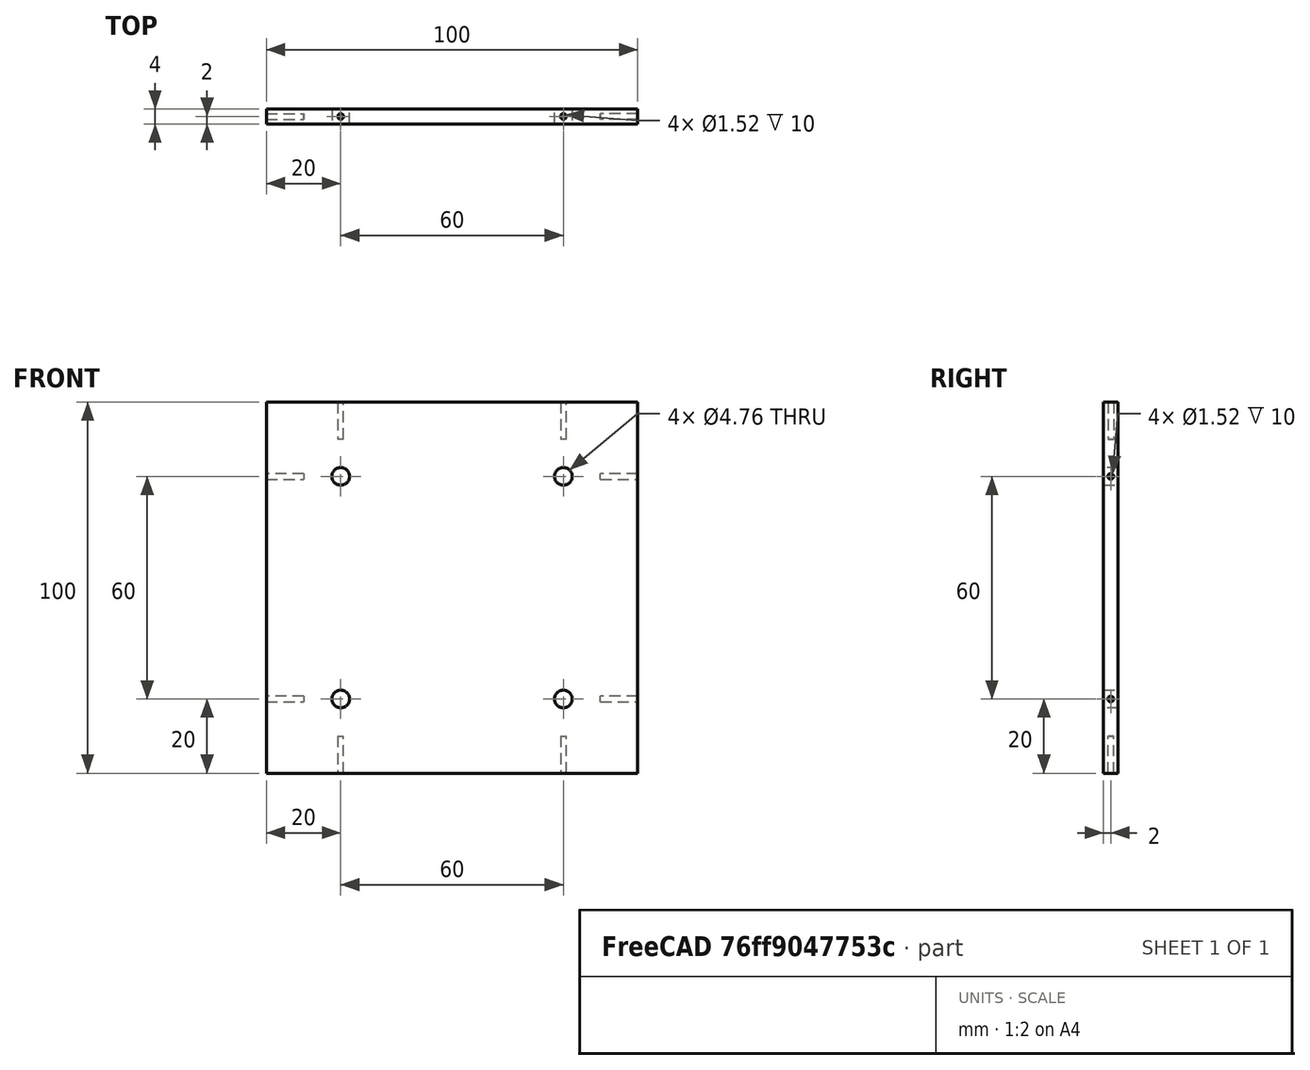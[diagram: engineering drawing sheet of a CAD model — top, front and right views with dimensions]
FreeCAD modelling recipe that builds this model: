
FCSTD DOCUMENT  (FreeCAD 0.20R29603 (Git))
Label: MechanicalCF35Mount002
License: All rights reserved
LicenseURL: http://en.wikipedia.org/wiki/All_rights_reserved
objects: Part::Cylinder×12, Part::Compound×9, TechDraw::DrawViewDimension×9, TechDraw::DrawProjGroupItem×5, Part::Cut×2, Part::Box×1, Part::Feature×1, TechDraw::DrawSVGTemplate×1, TechDraw::DrawProjGroup×1, TechDraw::DrawPage×1
note: 25 computed .brp shape members not serialized (recipe doc carries the construction recipe); baked Part::Feature solids carry a one-line shape summary decoded from their .brp

FEATURE [Part::Box] Box  label="Würfel"
  AttacherType = Attacher::AttachEngine3D
  Height = 100
  Length = 100
  Placement = pos=(-50,0,-50) rot=(0,0,1;0rad)
  Width = 4
FEATURE [Part::Cylinder] Cylinder011  label="Zylinder011"
  Angle = 360
  AttacherType = Attacher::AttachEngine3D
  FirstAngle = 0
  Height = 300
  Placement = pos=(30,12.7,30) rot=(1,0,0;1.5708rad)
  Radius = 2.38
  SecondAngle = 0
FEATURE [Part::Cylinder] Cylinder012  label="Zylinder012"
  Angle = 360
  AttacherType = Attacher::AttachEngine3D
  FirstAngle = 0
  Height = 300
  Placement = pos=(30,12.7,30) rot=(1,0,0;1.5708rad)
  Radius = 2.38
  SecondAngle = 0
FEATURE [Part::Compound] Compound008
  Links = -> [Cylinder012]
  Placement = pos=(0,0,0) rot=(0,1,0;1.5708rad)
FEATURE [Part::Cylinder] Cylinder013  label="Zylinder013"
  Angle = 360
  AttacherType = Attacher::AttachEngine3D
  FirstAngle = 0
  Height = 300
  Placement = pos=(30,12.7,30) rot=(1,0,0;1.5708rad)
  Radius = 2.38
  SecondAngle = 0
FEATURE [Part::Compound] Compound009
  Links = -> [Cylinder013]
  Placement = pos=(0,0,0) rot=(0,1,0;3.14159rad)
FEATURE [Part::Cylinder] Cylinder014  label="Zylinder014"
  Angle = 360
  AttacherType = Attacher::AttachEngine3D
  FirstAngle = 0
  Height = 300
  Placement = pos=(30,12.7,30) rot=(1,0,0;1.5708rad)
  Radius = 2.38
  SecondAngle = 0
FEATURE [Part::Compound] Compound010
  Links = -> [Cylinder014]
  Placement = pos=(0,0,0) rot=(0,-1,0;1.5708rad)
FEATURE [Part::Compound] Compound014  label="M6ThreadRods"
  Links = -> [Cylinder011,Compound008,Compound009,Compound010]
FEATURE [Part::Cut] Cut
  Base = -> Box
  Tool = -> Compound014
FEATURE [Part::Cylinder] Cylinder  label="Zylinder"
  Angle = 360
  AttacherType = Attacher::AttachEngine3D
  FirstAngle = 0
  Height = 10
  Placement = pos=(30,2,40) rot=(0,0,1;0rad)
  Radius = 0.76
  SecondAngle = 0
FEATURE [Part::Cylinder] Cylinder015  label="Zylinder015"
  Angle = 360
  AttacherType = Attacher::AttachEngine3D
  FirstAngle = 0
  Height = 10
  Placement = pos=(-30,2,40) rot=(0,0,1;0rad)
  Radius = 0.76
  SecondAngle = 0
FEATURE [Part::Compound] Compound
  Links = -> [Cylinder,Cylinder015]
FEATURE [Part::Cylinder] Cylinder016  label="Zylinder016"
  Angle = 360
  AttacherType = Attacher::AttachEngine3D
  FirstAngle = 0
  Height = 10
  Placement = pos=(30,2,40) rot=(0,0,1;0rad)
  Radius = 0.76
  SecondAngle = 0
FEATURE [Part::Cylinder] Cylinder017  label="Zylinder017"
  Angle = 360
  AttacherType = Attacher::AttachEngine3D
  FirstAngle = 0
  Height = 10
  Placement = pos=(-30,2,40) rot=(0,0,1;0rad)
  Radius = 0.76
  SecondAngle = 0
FEATURE [Part::Compound] Compound015
  Links = -> [Cylinder016,Cylinder017]
  Placement = pos=(0,0,0) rot=(0,1,0;1.5708rad)
FEATURE [Part::Cylinder] Cylinder018  label="Zylinder018"
  Angle = 360
  AttacherType = Attacher::AttachEngine3D
  FirstAngle = 0
  Height = 10
  Placement = pos=(30,2,40) rot=(0,0,1;0rad)
  Radius = 0.76
  SecondAngle = 0
FEATURE [Part::Cylinder] Cylinder019  label="Zylinder019"
  Angle = 360
  AttacherType = Attacher::AttachEngine3D
  FirstAngle = 0
  Height = 10
  Placement = pos=(-30,2,40) rot=(0,0,1;0rad)
  Radius = 0.76
  SecondAngle = 0
FEATURE [Part::Compound] Compound016
  Links = -> [Cylinder018,Cylinder019]
  Placement = pos=(0,0,0) rot=(0,1,0;3.14159rad)
FEATURE [Part::Cylinder] Cylinder020  label="Zylinder020"
  Angle = 360
  AttacherType = Attacher::AttachEngine3D
  FirstAngle = 0
  Height = 10
  Placement = pos=(30,2,40) rot=(0,0,1;0rad)
  Radius = 0.76
  SecondAngle = 0
FEATURE [Part::Cylinder] Cylinder021  label="Zylinder021"
  Angle = 360
  AttacherType = Attacher::AttachEngine3D
  FirstAngle = 0
  Height = 10
  Placement = pos=(-30,2,40) rot=(0,0,1;0rad)
  Radius = 0.76
  SecondAngle = 0
FEATURE [Part::Compound] Compound017
  Links = -> [Cylinder020,Cylinder021]
  Placement = pos=(0,0,0) rot=(0,-1,0;1.5708rad)
FEATURE [Part::Compound] Compound018  label="M2Corehole"
  Links = -> [Compound017,Compound,Compound015,Compound016]
FEATURE [Part::Cut] Cut001
  Base = -> Cut
  Tool = -> Compound018
FEATURE [Part::Feature] Cut001_solid  label="Cut001 (Solid)"
  shape: bbox 100 x 4 x 100 mm, 26 faces (baked)
FEATURE [TechDraw::DrawSVGTemplate] Template
  EditableTexts = Designed_by_Name=Thomas Spielauer; FC-Date=2023-07-05; FC-SC=mm; FC-SH=01; FC-Title=CF40 electronics housing; Subtitle=Backplate
  Height = 210
  Orientation = 1
  Width = 297
FEATURE [TechDraw::DrawProjGroupItem] ProjItem  label="Front"
  CoarseView = false
  Direction = (0,1,0)
  Focus = 100
  HardHidden = false
  IsoCount = 0
  IsoHidden = false
  IsoVisible = false
  LockPosition = true
  Perspective = false
  Rotation = 0
  RotationVector = (0,0,-1)
  ScaleType = 2
  SeamHidden = false
  SeamVisible = true
  SmoothHidden = false
  SmoothVisible = true
  Source = -> [Cut001]
  Type = 0
  X = 0
  XDirection = (0,0,-1)
  Y = 0
FEATURE [TechDraw::DrawProjGroupItem] ProjItem001  label="Right"
  CoarseView = false
  Direction = (0,1e-16,-1)
  Focus = 100
  HardHidden = false
  IsoCount = 0
  IsoHidden = false
  IsoVisible = false
  LockPosition = false
  Perspective = false
  Rotation = 0
  RotationVector = (1,0,0)
  ScaleType = 2
  SeamHidden = false
  SeamVisible = true
  SmoothHidden = false
  SmoothVisible = true
  Source = -> [Cut001]
  Type = 2
  X = -67.1947
  XDirection = (0,-1,-1e-16)
  Y = 0
FEATURE [TechDraw::DrawProjGroupItem] ProjItem002  label="Left"
  CoarseView = false
  Direction = (0,1e-16,1)
  Focus = 100
  HardHidden = false
  IsoCount = 0
  IsoHidden = false
  IsoVisible = false
  LockPosition = false
  Perspective = false
  Rotation = 0
  RotationVector = (1,0,0)
  ScaleType = 2
  SeamHidden = false
  SeamVisible = true
  SmoothHidden = false
  SmoothVisible = true
  Source = -> [Cut001]
  Type = 1
  X = 75.0685
  XDirection = (0,1,-1e-16)
  Y = 0
FEATURE [TechDraw::DrawProjGroupItem] ProjItem003  label="Bottom"
  CoarseView = false
  Direction = (1,0,0)
  Focus = 100
  HardHidden = false
  IsoCount = 0
  IsoHidden = false
  IsoVisible = false
  LockPosition = false
  Perspective = false
  Rotation = 0
  RotationVector = (1,0,0)
  ScaleType = 2
  SeamHidden = false
  SeamVisible = true
  SmoothHidden = false
  SmoothVisible = true
  Source = -> [Cut001]
  Type = 5
  X = 0
  XDirection = (0,0,-1)
  Y = 67.1947
FEATURE [TechDraw::DrawProjGroupItem] ProjItem004  label="Top"
  CoarseView = false
  Direction = (-1,0,0)
  Focus = 100
  HardHidden = false
  IsoCount = 0
  IsoHidden = false
  IsoVisible = false
  LockPosition = false
  Perspective = false
  Rotation = 0
  RotationVector = (1,0,0)
  ScaleType = 2
  SeamHidden = false
  SeamVisible = true
  SmoothHidden = false
  SmoothVisible = true
  Source = -> [Cut001]
  Type = 4
  X = 0
  XDirection = (0,0,-1)
  Y = -67.7571
FEATURE [TechDraw::DrawProjGroup] ProjGroup
  Anchor = -> ProjItem
  AutoDistribute = true
  LockPosition = false
  ProjectionType = 0
  Rotation = 0
  ScaleType = 0
  Source = -> [Cut001]
  Views = -> [ProjItem,ProjItem001,ProjItem002,ProjItem003,ProjItem004]
  X = 92.8803
  Y = 118.668
  spacingX = 15
  spacingY = 15
FEATURE [TechDraw::DrawViewDimension] Dimension
  AngleOverride = false
  Arbitrary = false
  ArbitraryTolerances = false
  EqualTolerance = true
  ExtensionAngle = 0
  FormatSpec = %.2w
  FormatSpecOverTolerance = %+.2w
  FormatSpecUnderTolerance = %+.2w
  Inverted = false
  LineAngle = 0
  LockPosition = false
  MeasureType = 1
  OverTolerance = 0
  References2D = -> [ProjItem002]
  Rotation = 0
  ScaleType = 0
  TheoreticalExact = false
  Type = 0
  UnderTolerance = 0
  X = 18.1793
  Y = 2.5
FEATURE [TechDraw::DrawViewDimension] Dimension001
  AngleOverride = false
  Arbitrary = false
  ArbitraryTolerances = false
  EqualTolerance = true
  ExtensionAngle = 0
  FormatSpec = %.2w
  FormatSpecOverTolerance = %+.2w
  FormatSpecUnderTolerance = %+.2w
  Inverted = false
  LineAngle = 0
  LockPosition = false
  MeasureType = 1
  OverTolerance = 0
  References2D = -> [ProjItem002]
  Rotation = 0
  ScaleType = 0
  TheoreticalExact = false
  Type = 0
  UnderTolerance = 0
  X = -0.392399
  Y = 61.2636
FEATURE [TechDraw::DrawViewDimension] Dimension002
  AngleOverride = false
  Arbitrary = false
  ArbitraryTolerances = false
  EqualTolerance = true
  ExtensionAngle = 0
  FormatSpec = %.2w
  FormatSpecOverTolerance = %+.2w
  FormatSpecUnderTolerance = %+.2w
  Inverted = false
  LineAngle = 0
  LockPosition = false
  MeasureType = 1
  OverTolerance = 0
  References2D = -> [ProjItem]
  Rotation = 0
  ScaleType = 0
  TheoreticalExact = false
  Type = 0
  UnderTolerance = 0
  X = 44.1743
  Y = -37.5
FEATURE [TechDraw::DrawViewDimension] Dimension003
  AngleOverride = false
  Arbitrary = false
  ArbitraryTolerances = false
  EqualTolerance = true
  ExtensionAngle = 0
  FormatSpec = %.2w
  FormatSpecOverTolerance = %+.2w
  FormatSpecUnderTolerance = %+.2w
  Inverted = false
  LineAngle = 0
  LockPosition = false
  MeasureType = 1
  OverTolerance = 0
  References2D = -> [ProjItem]
  Rotation = 0
  ScaleType = 0
  TheoreticalExact = false
  Type = 0
  UnderTolerance = 0
  X = 40.3767
  Y = -18.0345
FEATURE [TechDraw::DrawViewDimension] Dimension004
  AngleOverride = false
  Arbitrary = false
  ArbitraryTolerances = false
  EqualTolerance = true
  ExtensionAngle = 0
  FormatSpec = %.2w
  FormatSpecOverTolerance = %+.2w
  FormatSpecUnderTolerance = %+.2w
  Inverted = false
  LineAngle = 0
  LockPosition = false
  MeasureType = 1
  OverTolerance = 0
  References2D = -> [ProjItem004]
  Rotation = 0
  ScaleType = 0
  TheoreticalExact = false
  Type = 0
  UnderTolerance = 0
  X = -0.2616
  Y = -12.0568
FEATURE [TechDraw::DrawViewDimension] Dimension005
  AngleOverride = false
  Arbitrary = false
  ArbitraryTolerances = false
  EqualTolerance = true
  ExtensionAngle = 0
  FormatSpec = ⌀%.2w (4x)
  FormatSpecOverTolerance = %+.2w
  FormatSpecUnderTolerance = %+.2w
  Inverted = false
  LineAngle = 0
  LockPosition = false
  MeasureType = 1
  OverTolerance = 0
  References2D = -> [ProjItem]
  Rotation = 0
  ScaleType = 0
  TheoreticalExact = false
  Type = 5
  UnderTolerance = 0
  X = -14.8914
  Y = -16.9228
FEATURE [TechDraw::DrawViewDimension] Dimension006
  AngleOverride = false
  Arbitrary = false
  ArbitraryTolerances = false
  EqualTolerance = true
  ExtensionAngle = 0
  FormatSpec = %.2w
  FormatSpecOverTolerance = %+.2w
  FormatSpecUnderTolerance = %+.2w
  Inverted = false
  LineAngle = 0
  LockPosition = false
  MeasureType = 1
  OverTolerance = 0
  References2D = -> [ProjItem002]
  Rotation = 0
  ScaleType = 0
  TheoreticalExact = false
  Type = 0
  UnderTolerance = 0
  X = -9.2228
  Y = -18.7975
FEATURE [TechDraw::DrawViewDimension] Dimension007
  AngleOverride = false
  Arbitrary = false
  ArbitraryTolerances = false
  EqualTolerance = true
  ExtensionAngle = 0
  FormatSpec = %.2w
  FormatSpecOverTolerance = %+.2w
  FormatSpecUnderTolerance = %+.2w
  Inverted = false
  LineAngle = 0
  LockPosition = false
  MeasureType = 1
  OverTolerance = 0
  References2D = -> [ProjItem002]
  Rotation = 0
  ScaleType = 0
  TheoreticalExact = false
  Type = 0
  UnderTolerance = 0
  X = -11.0338
  Y = -36.7557
FEATURE [TechDraw::DrawViewDimension] Dimension008
  AngleOverride = false
  Arbitrary = false
  ArbitraryTolerances = false
  EqualTolerance = true
  ExtensionAngle = 0
  FormatSpec = ⌀%.2w
  FormatSpecOverTolerance = %+.2w
  FormatSpecUnderTolerance = %+.2w
  Inverted = false
  LineAngle = 0
  LockPosition = false
  MeasureType = 1
  OverTolerance = 0
  References2D = -> [ProjItem002]
  Rotation = 0
  ScaleType = 0
  TheoreticalExact = false
  Type = 5
  UnderTolerance = 0
  X = 12.2078
  Y = 35.5126
FEATURE [TechDraw::DrawPage] Page
  KeepUpdated = true
  NextBalloonIndex = 1
  ProjectionType = 0
  Template = -> Template
  Views = -> [ProjGroup,Dimension,Dimension001,Dimension002,Dimension003,Dimension004,Dimension005,Dimension006,Dimension007,Dimension008]
